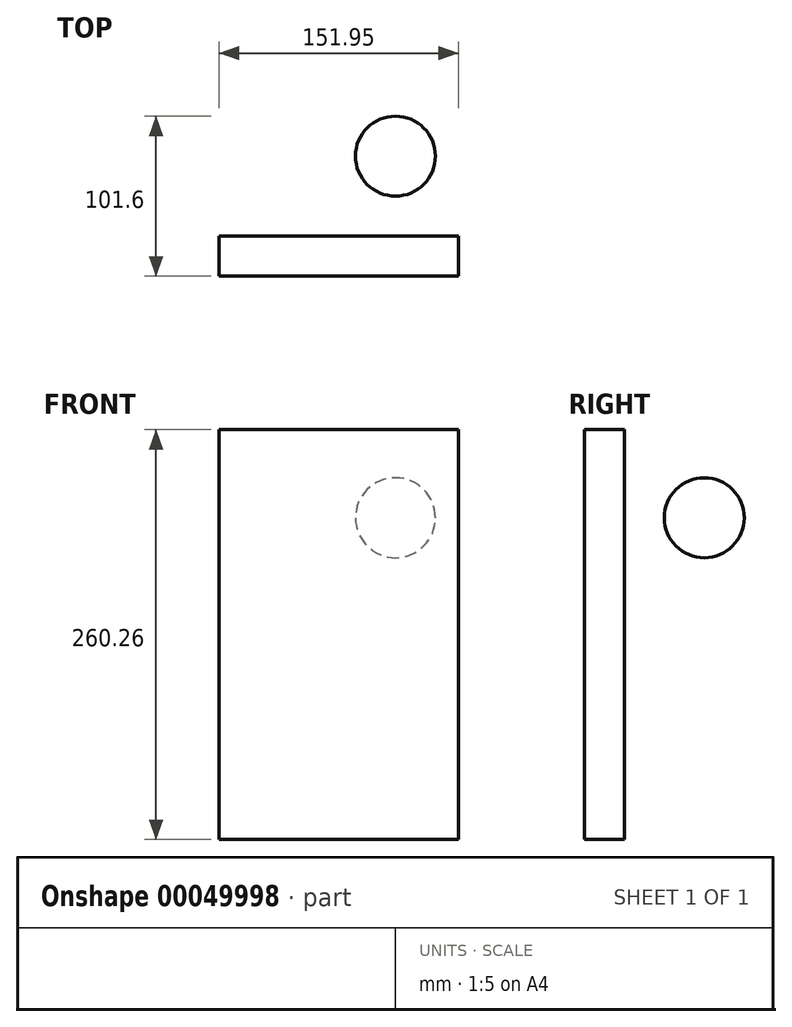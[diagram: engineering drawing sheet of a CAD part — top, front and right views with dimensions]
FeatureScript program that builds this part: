
annotation { "Feature Type Name" : "Feature", "Feature Type Description" : "" }
export const myFeature = defineFeature(function(context is Context, id is Id, definition is map)
    precondition{}
    {
        {
            var Q0;
            Q0=qCreatedBy(makeId("Front.planeOp"),FACE);
            var sketch = newSketch(context, id + "F0", { "sketchPlane" : qUnion([Q0])});
            skArc(sketch, "E0", {"start": v(25.4, 0) * mm, "mid": v(0, 25.4) * mm, "end": v(-25.4, 0) * mm});
            skLineSegment(sketch, "E1", {"start": v(-25.4, 0) * mm, "end": v(25.4, 0) * mm});
            skSolve(sketch);
        }
        {
            var Q0;
            Q0=makeQuery(id+"F0.imprint","IMPRINT",FACE,{"disambiguationData":[TD([[makeQuery(id+"F0.imprint","IMPRINT",EDGE,{"derivedFrom":sQuery(id+"F0.wireOp",EDGE,"E0")}),1.0]])]});
            var Q1;
            Q1=sQuery(id+"F0.wireOp",EDGE,"E1");
            revolve(context, id + "F1", {"entities" : qUnion([Q0]), "axis" : qUnion([Q1]), "revolveType" : RevolveType.FULL});
        }
        {
            var Q0;
            Q0=qCreatedBy(makeId("Front.planeOp"),FACE);
            cPlane(context, id + "F2", {"entities" : qUnion([Q0]), "cplaneType" : CPlaneType.OFFSET, "offset" : 50.8 * mm, "width" : 152.4 * mm, "height" : 152.4 * mm});
        }
        {
            var Q0;
            Q0=qCreatedBy(id+"F2.planeOp",FACE);
            var sketch = newSketch(context, id + "F3", { "sketchPlane" : qUnion([Q0])});
            skLineSegment(sketch, "E2.rect.bottom", {"start": v(39.97, 56) * mm, "end": v(-111.98, 56) * mm});
            skLineSegment(sketch, "E2.rect.top", {"start": v(39.97, -204.27) * mm, "end": v(-111.98, -204.27) * mm});
            skLineSegment(sketch, "E2.rect.left", {"start": v(39.97, 56) * mm, "end": v(39.97, -204.27) * mm});
            skLineSegment(sketch, "E2.rect.right", {"start": v(-111.98, 56) * mm, "end": v(-111.98, -204.27) * mm});
            skPoint(sketch, "E2.rect.middle", {"position": v(-36, -74.14) * mm});
            skSolve(sketch);
        }
        {
            var Q0;
            Q0 = qSketchRegion(id + "F3", true);
            extrude(context, id + "F4", {"entities" : qUnion([Q0]), "depth" : 25.4 * mm});
        }
    });
